FCSTD DOCUMENT  (FreeCAD 0.20R29177 +426 (Git))
Label: ASM_Base
License: All rights reserved
LicenseURL: http://en.wikipedia.org/wiki/All_rights_reserved
objects: App::Link×6, App::DocumentObjectGroup×3, PartDesign::CoordinateSystem×1, App::FeaturePython×1, App::Part×1
note: 1 computed .brp shape members not serialized (recipe doc carries the construction recipe); baked Part::Feature solids carry a one-line shape summary decoded from their .brp
EXTERNAL_REF file=CeilingPlate.FCStd obj=LCS_Origin
EXTERNAL_REF file=PipeFloorFlange.FCStd obj=LCS_1
EXTERNAL_REF file=PipeFloorFlange.FCStd obj=Body
EXTERNAL_REF file=PipeNipple.FCStd obj=LCS_root
EXTERNAL_REF file=PipeNipple.FCStd obj=Body
EXTERNAL_REF file=PipeNipple.FCStd obj=LCS_end
EXTERNAL_REF file=SlipRing.FCStd obj=LCS_Origin
EXTERNAL_REF file=SlipRing.FCStd obj=Assembly
EXTERNAL_REF file=CeilingPlate.FCStd obj=Assembly
EXTERNAL_REF file=CeilingPlate.FCStd obj=Pad
EXTERNAL_REF file=CeilingPlate.FCStd obj=Sketch001
EXTERNAL_REF file=StrutChannelHalf.FCStd obj=LCS_Face
EXTERNAL_REF file=StrutChannelHalf.FCStd obj=Assembly

FEATURE [App::DocumentObjectGroup] Parts
FEATURE [PartDesign::CoordinateSystem] LCS_Origin
  AttacherType = Attacher::AttachEngine3D
  MapMode = 2
  Support = -> [X_Axis]
FEATURE [App::FeaturePython] Variables  # WARN: FeaturePython — macro-defined, semantics opaque (R4)
  Type = App::PropertyContainer
FEATURE [App::DocumentObjectGroup] Constraints
FEATURE [App::DocumentObjectGroup] Configurations
FEATURE [App::Link] PipeFlange
  AssemblyType = Part::Link
  AttachedBy = #LCS_1
  AttachedTo = CeilingPlate#LCS_Origin
  AttachmentOffset = pos=(0,0,0) rot=(1,0,0;3.14159rad)
  LinkPlacement = pos=(0,0,0) rot=(1,0,0;3.14159rad)
  LinkedObject = -> <external PipeFloorFlange.FCStd>#Body
  Placement = pos=(0,0,0) rot=(1,0,0;3.14159rad)
  SolverId = Asm4EE
  expr: Placement = CeilingPlate.Placement * CeilingPlate#LCS_Origin.Placement * AttachmentOffset * PipeFloorFlange#LCS_1.Placement ^ -1
FEATURE [App::Link] PipeNipple
  AssemblyType = Part::Link
  AttachedBy = #LCS_root
  AttachedTo = PipeFlange#LCS_1
  LinkPlacement = pos=(0,0,0) rot=(1,0,0;3.14159rad)
  LinkedObject = -> <external PipeNipple.FCStd>#Body
  Placement = pos=(0,0,0) rot=(1,0,0;3.14159rad)
  SolverId = Asm4EE
  expr: Placement = PipeFlange.Placement * PipeFloorFlange#LCS_1.Placement * AttachmentOffset * PipeNipple#LCS_root.Placement ^ -1
FEATURE [App::Link] SlipRing
  AttachedBy = #LCS_Origin
  AttachedTo = PipeNipple#LCS_end
  AttachmentOffset = pos=(0,0,0) rot=(1,0,0;3.14159rad)
  LinkPlacement = pos=(0,-1.09e-14,-88.9) rot=(0,0,1;0rad)
  LinkedObject = -> <external SlipRing.FCStd>#Assembly
  Placement = pos=(0,-1.09e-14,-88.9) rot=(0,0,1;0rad)
  SolverId = Asm4EE
  expr: Placement = PipeNipple.Placement * PipeNipple#LCS_end.Placement * AttachmentOffset * SlipRing#LCS_Origin.Placement ^ -1
FEATURE [App::Link] CeilingPlate
  AttachedBy = #LCS_Origin
  AttachedTo = Parent Assembly#LCS_Origin
  LinkedObject = -> <external CeilingPlate.FCStd>#Assembly
  SolverId = Asm4EE
  expr: Placement = LCS_Origin.Placement * AttachmentOffset * CeilingPlate#LCS_Origin.Placement ^ -1
FEATURE [App::Link] StrutChannelHalf
  AttachedBy = #LCS_Face
  AttachedTo = Parent Assembly#LCS_Origin
  AttachmentOffset = pos=(135.057,0,18.5) rot=(1,0,0;4.71239rad)
  LinkPlacement = pos=(135.057,4.6e-15,39.14) rot=(1,0,0;4.71239rad)
  LinkedObject = -> <external StrutChannelHalf.FCStd>#Assembly
  Placement = pos=(135.057,4.6e-15,39.14) rot=(1,0,0;4.71239rad)
  SolverId = Asm4EE
  expr: .AttachmentOffset.Base.x = <<CeilingPlate>>#<<Sketch001>>.Constraints.CeilingRailSpacing / 2
  expr: .AttachmentOffset.Base.z = <<CeilingPlate>>#<<Pad>>.Length
  expr: Placement = LCS_Origin.Placement * AttachmentOffset * StrutChannelHalf#LCS_Face.Placement ^ -1
FEATURE [App::Link] StrutChannelHalf001
  AttachedBy = #LCS_Face
  AttachedTo = Parent Assembly#LCS_Origin
  AttachmentOffset = pos=(-135.057,0,18.5) rot=(1,0,0;4.71239rad)
  LinkPlacement = pos=(-135.057,4.6e-15,39.14) rot=(1,0,0;4.71239rad)
  LinkedObject = -> <external StrutChannelHalf.FCStd>#Assembly
  Placement = pos=(-135.057,4.6e-15,39.14) rot=(1,0,0;4.71239rad)
  SolverId = Asm4EE
  expr: .AttachmentOffset.Base.x = <<CeilingPlate>>#<<Sketch001>>.Constraints.CeilingRailSpacing / -2
  expr: .AttachmentOffset.Base.z = <<CeilingPlate>>#<<Pad>>.Length
  expr: Placement = LCS_Origin.Placement * AttachmentOffset * StrutChannelHalf#LCS_Face.Placement ^ -1
FEATURE [App::Part] Assembly
  AssemblyType = Part::Link
  Group = -> [LCS_Origin,Variables,Constraints,Configurations,PipeFlange,PipeNipple,SlipRing,CeilingPlate,StrutChannelHalf,StrutChannelHalf001]
  LabelDocUser = ASM_Base
  LabelPartUser = Assembly
  Origin = -> Origin
  Type = Assembly

RESOLVED EXTERNAL PARTS (link-assembly join: the EXTERNAL_REF files above that resolve inside this repo's crawl, each included once):
---- part CeilingPlate.FCStd = doc fcstd_5e722962f203 ----
FCSTD DOCUMENT  (FreeCAD 0.20R29177 +426 (Git))
Label: CeilingPlate
License: All rights reserved
LicenseURL: http://en.wikipedia.org/wiki/All_rights_reserved
objects: App::DocumentObjectGroup×4, Sketcher::SketchObject×2, Part::FeaturePython×2, PartDesign::CoordinateSystem×1, App::FeaturePython×1, PartDesign::Pad×1, PartDesign::Hole×1, PartDesign::Body×1, App::Part×1
note: 10 computed .brp shape members not serialized (recipe doc carries the construction recipe); baked Part::Feature solids carry a one-line shape summary decoded from their .brp
EXTERNAL_REF file=Params.FCStd obj=Spreadsheet

FEATURE [App::DocumentObjectGroup] Parts
FEATURE [PartDesign::CoordinateSystem] LCS_Origin
  AttacherType = Attacher::AttachEngine3D
  MapMode = 2
  Support = -> [X_Axis]
FEATURE [App::FeaturePython] Variables  # WARN: FeaturePython — macro-defined, semantics opaque (R4)
  Type = App::PropertyContainer
FEATURE [App::DocumentObjectGroup] Constraints
FEATURE [App::DocumentObjectGroup] Configurations
FEATURE [Sketcher::SketchObject] Sketch
  FullyConstrained = true
  MapMode = 5
  Support = -> [XY_Plane001]
  expr: .Constraints.Diameter = <<Params>>#<<Params>>.CeilingPlateDiameter
  sketch-geometry (2):
    g0: Circle CenterX=0 CenterY=0 CenterZ=0 NormalX=0 NormalY=0 NormalZ=1 AngleXU=0 Radius=12.5
    g1: Circle CenterX=0 CenterY=0 CenterZ=0 NormalX=0 NormalY=0 NormalZ=1 AngleXU=0 Radius=231.5
  constraints (4):
    c: Coincident(g0,g-1)
    c: Coincident(g1,g0)
    c: Diameter(g1) = 463  'Diameter'
    c: Diameter(g0) = 25
FEATURE [PartDesign::Pad] Pad
  Direction = (0,0,1)
  Length = 18.5
  Length2 = 10
  Profile = -> Sketch
  ReferenceAxis = -> Sketch [N_Axis]
  Type = 0
  expr: Length = <<Params>>#<<Params>>.PlywoodThickness
FEATURE [Sketcher::SketchObject] Sketch001
  FullyConstrained = true
  MapMode = 5
  Support = -> [XY_Plane001]
  expr: Constraints[15] = <<Params>>#<<Params>>.TableRollerDriveSupportRadius
  expr: Constraints[16] = <<Params>>#<<Params>>.TableRollerSideRadius
  sketch-geometry (12):
    g0: Circle CenterX=135.057 CenterY=135.057 CenterZ=0 NormalX=0 NormalY=0 NormalZ=1 AngleXU=0 Radius=2.5
    g1: LineSegment StartX=-135.057 StartY=-135.057 StartZ=0 EndX=-135.057 EndY=135.057 EndZ=0
    g2: LineSegment StartX=-135.057 StartY=135.057 StartZ=0 EndX=135.057 EndY=135.057 EndZ=0
    g3: LineSegment StartX=135.057 StartY=135.057 StartZ=0 EndX=135.057 EndY=-135.057 EndZ=0
    g4: LineSegment StartX=135.057 StartY=-135.057 StartZ=0 EndX=-135.057 EndY=-135.057 EndZ=0
    g5: GeomPoint X=0 Y=0 Z=0
    g6: Circle CenterX=0 CenterY=0 CenterZ=0 NormalX=0 NormalY=0 NormalZ=1 AngleXU=0 Radius=218
    g7: Circle CenterX=0 CenterY=0 CenterZ=0 NormalX=0 NormalY=0 NormalZ=1 AngleXU=0 Radius=164
    g8: LineSegment StartX=115.966 StartY=115.966 StartZ=0 EndX=154.149 EndY=154.149 EndZ=0
    g9: Circle CenterX=-135.057 CenterY=135.057 CenterZ=0 NormalX=0 NormalY=0 NormalZ=1 AngleXU=0 Radius=2.5
    g10: Circle CenterX=-135.057 CenterY=-135.057 CenterZ=0 NormalX=0 NormalY=0 NormalZ=1 AngleXU=0 Radius=2.5
    g11: Circle CenterX=135.057 CenterY=-135.057 CenterZ=0 NormalX=0 NormalY=0 NormalZ=1 AngleXU=0 Radius=2.5
  constraints (28):
    c: Coincident(g1,g2)
    c: Coincident(g2,g3)
    c: Coincident(g3,g4)
    c: Coincident(g4,g1)
    c: Horizontal(g2)
    c: Horizontal(g4)
    c: Vertical(g1)
    c: Vertical(g3)
    c: Symmetric(g2,g1,g5)
    c: Coincident(g5,g-1)
    c: Coincident(g2,g0)
    c: Equal(g3,g2)
    c: Diameter(g0) = 5
    c: Coincident(g6,g5)
    c: Coincident(g7,g5)
    c: Radius(g6) = 218
    c: Radius(g7) = 164
    c: PointOnObject(g8,g7)
    c: PointOnObject(g8,g6)
    c: PointOnObject(g5,g8)
    c: Symmetric(g8,g8,g0)
    c: Coincident(g9,g1)
    c: Coincident(g10,g1)
    c: Coincident(g11,g3)
    c: Equal(g10,g11)
    c: Equal(g11,g9)
    c: Equal(g9,g0)
    c: DistanceX(g2,g2) = 270.115  'CeilingRailSpacing'
FEATURE [PartDesign::Hole] Hole  label="MountHoles"
  BaseFeature = -> Pad
  CustomThreadClearance = 0
  Depth = 1342.04
  DepthType = 1
  Diameter = 10.3
  DrillForDepth = false
  DrillPoint = 1
  DrillPointAngle = 118
  HoleCutCountersinkAngle = 82
  HoleCutCustomValues = false
  HoleCutDepth = 1.5
  HoleCutDiameter = 20.3
  HoleCutType = 2
  ModelThread = false
  Profile = -> Sketch001
  Reversed = true
  Tapered = false
  TaperedAngle = 90
  ThreadClass = 0
  ThreadDepth = 1342.04
  ThreadDepthType = 0
  ThreadDirection = 0
  ThreadFit = 0
  ThreadSize = 11
  ThreadType = 3
  Threaded = false
  UseCustomThreadClearance = false
FEATURE [PartDesign::Body] Body
  Group = -> [Sketch,Pad,Sketch001,Hole]
  Origin = -> Origin001
  Tip = -> Hole
FEATURE [Part::FeaturePython] Screw  label="3/8inx1 1/4in-Screw"  # Fasteners workbench fastener (typed FeaturePython)
  Placement = pos=(135.057,-135.057,0) rot=(1,0,0;3.14159rad)
  baseObject = -> Sketch001 [Edge4]
  diameter = 12
  invert = true
  leftHanded = false
  length = 3
  lengthCustom = 31.75
  matchOuter = false
  offset = 0
  thread = false
  type = 3
FEATURE [Part::FeaturePython] Array_Screw  label="Array_3/8inx1 1/4in-Screw"  # Draft array (typed FeaturePython)
  ArraySteps = 0
  ArrayType = Circular Array
  Axis = LCS_Origin.Z
  Count = 4
  ElementCount = 4
  FullAngle = 360
  IntervalAngle = 90
  LinearSteps = 0
  PlacementList = 4 placements: [(135.057,-135.057,0),(135.057,135.057,0),(-135.057,135.057,0),(-135.057,-135.057,0)]
  ScaleList = (4) [(1,1,1),(1,1,1),(1,1,1),(1,1,1)]
  ShowElement = false
  SourceObject = -> Screw
FEATURE [App::DocumentObjectGroup] Fasteners
  Group = -> [Screw,Array_Screw]
FEATURE [App::Part] Assembly
  AssemblyType = Part::Link
  Group = -> [LCS_Origin,Variables,Constraints,Configurations,Body,Fasteners,Screw,Array_Screw]
  Origin = -> Origin
  Type = Assembly
---- part PipeFloorFlange.FCStd = doc fcstd_2355635570af ----
FCSTD DOCUMENT  (FreeCAD 0.20R29177 +426 (Git))
Label: PipeFloorFlange
License: All rights reserved
LicenseURL: http://en.wikipedia.org/wiki/All_rights_reserved
objects: Sketcher::SketchObject×2, PartDesign::Revolution×1, PartDesign::Hole×1, PartDesign::PolarPattern×1, PartDesign::CoordinateSystem×1, PartDesign::Body×1
note: 9 computed .brp shape members not serialized (recipe doc carries the construction recipe); baked Part::Feature solids carry a one-line shape summary decoded from their .brp

FEATURE [Sketcher::SketchObject] Sketch
  FullyConstrained = true
  MapMode = 5
  Placement = pos=(0,0,0) rot=(1,0,0;1.5708rad)
  Support = -> [XZ_Plane]
  sketch-geometry (6):
    g0: LineSegment StartX=14.86 StartY=0 StartZ=0 EndX=47.625 EndY=0 EndZ=0
    g1: LineSegment StartX=47.625 StartY=0 StartZ=0 EndX=47.625 EndY=8 EndZ=0
    g2: LineSegment StartX=47.625 StartY=8 StartZ=0 EndX=22.86 EndY=8 EndZ=0
    g3: LineSegment StartX=22.86 StartY=8 StartZ=0 EndX=22.86 EndY=17.78 EndZ=0
    g4: LineSegment StartX=22.86 StartY=17.78 StartZ=0 EndX=14.86 EndY=17.78 EndZ=0
    g5: LineSegment StartX=14.86 StartY=17.78 StartZ=0 EndX=14.86 EndY=0 EndZ=0
  constraints (18):
    c: PointOnObject(g0,g-1)
    c: Horizontal(g0)
    c: Coincident(g1,g0)
    c: Coincident(g2,g1)
    c: Horizontal(g2)
    c: Coincident(g3,g2)
    c: Vertical(g3)
    c: Coincident(g4,g3)
    c: Horizontal(g4)
    c: Vertical(g5)
    c: Coincident(g5,g4)
    c: Coincident(g5,g0)
    c: Vertical(g1)
    c: DistanceX(g-1,g3) = 22.86
    c: DistanceY(g1,g1) = 8  'Thickness'
    c: DistanceY(g5,g5) = 17.78
    c: DistanceX(g-1,g0) = 47.625
    c: DistanceX(g4,g4) = 8
FEATURE [PartDesign::Revolution] Revolution
  Angle = 360
  Axis = (0,-2e-16,1)
  Base = (0,0,0)
  Placement = pos=(0,0,0) rot=(1,0,0;1.5708rad)
  Profile = -> Sketch
  ReferenceAxis = -> Sketch [V_Axis]
  Reversed = true
FEATURE [Sketcher::SketchObject] Sketch001
  AttachmentOffset = pos=(0,0,8) rot=(0,0,1;0rad)
  FullyConstrained = true
  MapMode = 5
  Placement = pos=(0,0,8) rot=(0,0,1;0rad)
  Support = -> [XY_Plane]
  expr: .AttachmentOffset.Base.z = <<Sketch>>.Constraints.Thickness
  sketch-geometry (1):
    g0: Circle CenterX=0 CenterY=35 CenterZ=0 NormalX=0 NormalY=0 NormalZ=1 AngleXU=0 Radius=3
  constraints (3):
    c: PointOnObject(g0,g-2)
    c: DistanceY(g-1,g0) = 35
    c: Diameter(g0) = 6
FEATURE [PartDesign::Hole] Hole
  BaseFeature = -> Revolution
  CustomThreadClearance = 0
  Depth = 25
  DepthType = 0
  Diameter = 8.7
  DrillForDepth = false
  DrillPoint = 1
  DrillPointAngle = 118
  HoleCutCountersinkAngle = 82
  HoleCutCustomValues = false
  HoleCutDepth = 0
  HoleCutDiameter = 14.79
  HoleCutType = 2
  ModelThread = false
  Placement = pos=(0,0,0) rot=(1,0,0;1.5708rad)
  Profile = -> Sketch001
  Tapered = false
  TaperedAngle = 90
  ThreadClass = 0
  ThreadDepth = 25
  ThreadDepthType = 0
  ThreadDirection = 0
  ThreadFit = 0
  ThreadSize = 10
  ThreadType = 3
  Threaded = false
  UseCustomThreadClearance = false
FEATURE [PartDesign::PolarPattern] PolarPattern
  Angle = 360
  Axis = -> Sketch001 [N_Axis]
  BaseFeature = -> Hole
  Occurrences = 4
  Originals = -> [Hole]
  Placement = pos=(0,0,0) rot=(1,0,0;1.5708rad)
FEATURE [PartDesign::CoordinateSystem] LCS_1
  AttacherType = Attacher::AttachEngine3D
  MapMode = 2
  Support = -> [XY_Plane]
FEATURE [PartDesign::Body] Body
  Group = -> [Sketch,Revolution,Sketch001,Hole,PolarPattern,LCS_1]
  Origin = -> Origin
  Tip = -> PolarPattern
---- part PipeNipple.FCStd = doc fcstd_4dfc671c1cfc ----
FCSTD DOCUMENT  (FreeCAD 0.20R29177 +426 (Git))
Label: PipeNipple
License: All rights reserved
LicenseURL: http://en.wikipedia.org/wiki/All_rights_reserved
objects: PartDesign::CoordinateSystem×2, Sketcher::SketchObject×1, PartDesign::Pad×1, PartDesign::Body×1
note: 6 computed .brp shape members not serialized (recipe doc carries the construction recipe); baked Part::Feature solids carry a one-line shape summary decoded from their .brp

FEATURE [Sketcher::SketchObject] Sketch
  FullyConstrained = true
  MapMode = 5
  Support = -> [XY_Plane]
  sketch-geometry (2):
    g0: Circle CenterX=0 CenterY=0 CenterZ=0 NormalX=0 NormalY=0 NormalZ=1 AngleXU=0 Radius=13.3223
    g1: Circle CenterX=0 CenterY=0 CenterZ=0 NormalX=0 NormalY=0 NormalZ=1 AngleXU=0 Radius=16.7005
  constraints (4):
    c: Coincident(g0,g-1)
    c: Coincident(g1,g0)
    c: Diameter(g1) = 33.401
    c: Diameter(g0) = 26.6446
FEATURE [PartDesign::Pad] Pad
  Direction = (0,0,1)
  Length = 88.9
  Length2 = 10
  Profile = -> Sketch
  ReferenceAxis = -> Sketch [N_Axis]
  Type = 0
FEATURE [PartDesign::CoordinateSystem] LCS_root
  AttacherType = Attacher::AttachEngine3D
  MapMode = 2
  Support = -> [XY_Plane]
FEATURE [PartDesign::CoordinateSystem] LCS_end
  AttacherType = Attacher::AttachEngine3D
  AttachmentOffset = pos=(0,0,88.9) rot=(0,0,1;0rad)
  MapMode = 2
  Placement = pos=(0,0,88.9) rot=(0,0,1;0rad)
  Support = -> [LCS_root]
  expr: .AttachmentOffset.Base.z = <<Pad>>.Length
FEATURE [PartDesign::Body] Body
  Group = -> [Sketch,Pad,LCS_root,LCS_end]
  Origin = -> Origin
  Tip = -> Pad
---- part SlipRing.FCStd = doc fcstd_0743c411564a ----
FCSTD DOCUMENT  (FreeCAD 0.20R29177 +426 (Git))
Label: SlipRing
License: All rights reserved
LicenseURL: http://en.wikipedia.org/wiki/All_rights_reserved
objects: App::DocumentObjectGroup×3, PartDesign::CoordinateSystem×1, App::FeaturePython×1, Sketcher::SketchObject×1, PartDesign::Revolution×1, PartDesign::Body×1, App::Part×1
note: 5 computed .brp shape members not serialized (recipe doc carries the construction recipe); baked Part::Feature solids carry a one-line shape summary decoded from their .brp

FEATURE [App::DocumentObjectGroup] Parts
FEATURE [PartDesign::CoordinateSystem] LCS_Origin
  AttacherType = Attacher::AttachEngine3D
  MapMode = 2
  Support = -> [X_Axis]
FEATURE [App::FeaturePython] Variables  # WARN: FeaturePython — macro-defined, semantics opaque (R4)
  Type = App::PropertyContainer
FEATURE [App::DocumentObjectGroup] Constraints
FEATURE [App::DocumentObjectGroup] Configurations
FEATURE [Sketcher::SketchObject] Sketch
  FullyConstrained = true
  MapMode = 5
  Placement = pos=(0,0,0) rot=(1,0,0;1.5708rad)
  Support = -> [XZ_Plane001]
  sketch-geometry (14):
    g0: LineSegment StartX=0 StartY=38.6 StartZ=0 EndX=11 EndY=38.6 EndZ=0
    g1: LineSegment StartX=11 StartY=38.6 StartZ=0 EndX=11 EndY=0 EndZ=0
    g2: LineSegment StartX=11 StartY=0 StartZ=0 EndX=22.2 EndY=0 EndZ=0
    g3: LineSegment StartX=22.2 StartY=0 StartZ=0 EndX=22.2 EndY=-2.6 EndZ=0
    g4: LineSegment StartX=22.2 StartY=-2.6 StartZ=0 EndX=11 EndY=-2.6 EndZ=0
    g5: LineSegment StartX=11 StartY=-2.6 StartZ=0 EndX=11 EndY=-8.6 EndZ=0
    g6: LineSegment StartX=11 StartY=-8.6 StartZ=0 EndX=5 EndY=-8.6 EndZ=0
    g7: LineSegment StartX=5 StartY=-8.6 StartZ=0 EndX=5 EndY=-14.6 EndZ=0
    g8: LineSegment StartX=0 StartY=-14.6 StartZ=0 EndX=0 EndY=38.6 EndZ=0
    g9: LineSegment StartX=5 StartY=-14.6 StartZ=0 EndX=4 EndY=-14.6 EndZ=0
    g10: LineSegment StartX=4 StartY=-14.6 StartZ=0 EndX=0 EndY=-14.6 EndZ=0
    g11: LineSegment StartX=4 StartY=-14.6 StartZ=0 EndX=4 EndY=-30.6 EndZ=0
    g12: LineSegment StartX=4 StartY=-30.6 StartZ=0 EndX=0 EndY=-30.6 EndZ=0
    g13: LineSegment StartX=0 StartY=-30.6 StartZ=0 EndX=0 EndY=-14.6 EndZ=0
  constraints (41):
    c: PointOnObject(g0,g-2)
    c: Horizontal(g0)
    c: Coincident(g0,g1)
    c: Vertical(g1)
    c: Coincident(g1,g2)
    c: Horizontal(g2)
    c: Coincident(g2,g3)
    c: Vertical(g3)
    c: Coincident(g3,g4)
    c: Horizontal(g4)
    c: Coincident(g4,g5)
    c: Vertical(g5)
    c: Coincident(g5,g6)
    c: Coincident(g6,g7)
    c: Vertical(g7)
    c: Coincident(g7,g9)
    c: PointOnObject(g10,g-2)
    c: Coincident(g10,g8)
    c: Coincident(g8,g0)
    c: Horizontal(g6)
    c: DistanceX(g0,g0) = 11
    c: DistanceX(g-1,g3) = 22.2
    c: PointOnObject(g1,g5)
    c: DistanceX(g10,g9) = 5
    c: DistanceY(g7,g7) = 6
    c: DistanceY(g5,g5) = 6
    c: DistanceY(g3,g3) = 2.6
    c: DistanceY(g1,g1) = 38.6
    c: PointOnObject(g1,g-1)
    c: Coincident(g9,g10)
    c: Horizontal(g9)
    c: Horizontal(g10)
    c: Coincident(g11,g9)
    c: Vertical(g11)
    c: Coincident(g12,g11)
    c: PointOnObject(g12,g-2)
    c: Horizontal(g12)
    c: Coincident(g13,g12)
    c: Coincident(g13,g8)
    c: DistanceX(g12,g12) = 4
    c: DistanceY(g13,g13) = 16
FEATURE [PartDesign::Revolution] Revolution
  Angle = 360
  Axis = (0,-2e-16,1)
  Base = (0,0,0)
  Placement = pos=(0,0,0) rot=(1,0,0;1.5708rad)
  Profile = -> Sketch
  ReferenceAxis = -> Sketch [V_Axis]
  Reversed = true
FEATURE [PartDesign::Body] Body
  Group = -> [Sketch,Revolution]
  Origin = -> Origin001
  Tip = -> Revolution
FEATURE [App::Part] Assembly
  AssemblyType = Part::Link
  Group = -> [LCS_Origin,Variables,Constraints,Configurations,Body]
  Origin = -> Origin
  Type = Assembly
---- part StrutChannelHalf.FCStd = doc fcstd_f8280f6d5164 ----
FCSTD DOCUMENT  (FreeCAD 0.20R29177 +426 (Git))
Label: StrutChannelHalf
License: All rights reserved
LicenseURL: http://en.wikipedia.org/wiki/All_rights_reserved
objects: App::DocumentObjectGroup×3, PartDesign::CoordinateSystem×2, Sketcher::SketchObject×2, App::FeaturePython×1, PartDesign::Pad×1, PartDesign::Pocket×1, PartDesign::LinearPattern×1, PartDesign::Mirrored×1, PartDesign::MultiTransform×1, PartDesign::Body×1, App::Part×1
note: 12 computed .brp shape members not serialized (recipe doc carries the construction recipe); baked Part::Feature solids carry a one-line shape summary decoded from their .brp

FEATURE [App::DocumentObjectGroup] Parts
FEATURE [PartDesign::CoordinateSystem] LCS_Origin
  AttacherType = Attacher::AttachEngine3D
  MapMode = 2
  Support = -> [X_Axis]
FEATURE [App::FeaturePython] Variables  # WARN: FeaturePython — macro-defined, semantics opaque (R4)
  Length = 600
  Type = App::PropertyContainer
FEATURE [App::DocumentObjectGroup] Constraints
FEATURE [App::DocumentObjectGroup] Configurations
FEATURE [Sketcher::SketchObject] Sketch
  FullyConstrained = true
  MapMode = 5
  Support = -> [XY_Plane001]
  sketch-geometry (22):
    g0: ArcOfCircle CenterX=-15.875 CenterY=15.8775 CenterZ=0 NormalX=0 NormalY=0 NormalZ=1 AngleXU=0 Radius=4.7625 StartAngle=-5.3e-15 EndAngle=3.14159
    g1: ArcOfCircle CenterX=15.875 CenterY=15.8775 CenterZ=0 NormalX=0 NormalY=0 NormalZ=1 AngleXU=0 Radius=4.7625 StartAngle=1e-16 EndAngle=3.14159
    g2: LineSegment StartX=20.6375 StartY=15.8775 StartZ=0 EndX=20.6375 EndY=1.5 EndZ=0
    g3: ArcOfCircle CenterX=19.1375 CenterY=1.5 CenterZ=0 NormalX=0 NormalY=0 NormalZ=1 AngleXU=0 Radius=1.5 StartAngle=4.71239 EndAngle=6.28319
    g4: LineSegment StartX=19.1375 StartY=0 StartZ=0 EndX=-19.1375 EndY=0 EndZ=0
    g5: ArcOfCircle CenterX=-19.1375 CenterY=1.5 CenterZ=0 NormalX=0 NormalY=0 NormalZ=1 AngleXU=0 Radius=1.5 StartAngle=3.14159 EndAngle=4.71239
    g6: LineSegment StartX=-20.6375 StartY=1.5 StartZ=0 EndX=-20.6375 EndY=15.8775 EndZ=0
    g7: GeomPoint X=20.6375 Y=0 Z=0
    g8: ArcOfCircle CenterX=-15.875 CenterY=15.8775 CenterZ=0 NormalX=0 NormalY=0 NormalZ=1 AngleXU=0 Radius=2.86512 StartAngle=-8e-15 EndAngle=3.14159
    g9: ArcOfCircle CenterX=15.875 CenterY=15.8775 CenterZ=0 NormalX=0 NormalY=0 NormalZ=1 AngleXU=0 Radius=2.86512 StartAngle=1e-16 EndAngle=3.14159
    g10: LineSegment StartX=18.7401 StartY=15.8775 StartZ=0 EndX=18.7401 EndY=2.89738 EndZ=0
    g11: ArcOfCircle CenterX=17.7401 CenterY=2.89738 CenterZ=0 NormalX=0 NormalY=0 NormalZ=1 AngleXU=0 Radius=1 StartAngle=4.71239 EndAngle=6.28319
    g12: LineSegment StartX=17.7401 StartY=1.89738 StartZ=0 EndX=-17.7401 EndY=1.89738 EndZ=0
    g13: ArcOfCircle CenterX=-17.7401 CenterY=2.89738 CenterZ=0 NormalX=0 NormalY=0 NormalZ=1 AngleXU=0 Radius=1 StartAngle=3.14159 EndAngle=4.71239
    g14: LineSegment StartX=-18.7401 StartY=2.89738 StartZ=0 EndX=-18.7401 EndY=15.8775 EndZ=0
    g15: GeomPoint X=18.7401 Y=1.89738 Z=0
    g16: GeomPoint X=1.3e-15 Y=1.89738 Z=0
    g17: LineSegment StartX=1.3e-15 StartY=1.89738 StartZ=0 EndX=0 EndY=0 EndZ=0
    g18: LineSegment StartX=18.7401 StartY=15.8775 StartZ=0 EndX=20.6375 EndY=15.8775 EndZ=0
    g19: LineSegment StartX=-13.0099 StartY=15.8775 StartZ=0 EndX=-11.1125 EndY=15.8775 EndZ=0
    g20: LineSegment StartX=11.1125 StartY=15.8775 StartZ=0 EndX=13.0099 EndY=15.8775 EndZ=0
    g21: LineSegment StartX=-15.875 StartY=20.64 StartZ=0 EndX=15.875 EndY=20.64 EndZ=0
  constraints (54):
    c: Tangent(g1,g2) = 1.5708
    c: Tangent(g2,g3) = 1.5708
    c: Tangent(g3,g4) = 1.5708
    c: Tangent(g4,g5) = 1.5708
    c: Tangent(g5,g6) = 1.5708
    c: Tangent(g6,g0) = 1.5708
    c: Horizontal(g4)
    c: Vertical(g2)
    c: Vertical(g6)
    c: Equal(g0,g1)
    c: Equal(g3,g5)
    c: PointOnObject(g7,g2)
    c: PointOnObject(g7,g4)
    c: Symmetric(g4,g3,g-1)
    c: Radius(g3) = 1.5
    c: Radius(g1) = 4.7625
    c: Tangent(g9,g10) = 1.5708
    c: Tangent(g10,g11) = 1.5708
    c: Tangent(g11,g12) = 1.5708
    c: Tangent(g12,g13) = 1.5708
    c: Tangent(g13,g14) = 1.5708
    c: Tangent(g14,g8) = 1.5708
    c: Horizontal(g12)
    c: Vertical(g10)
    c: Vertical(g14)
    c: Equal(g8,g9)
    c: Equal(g11,g13)
    c: PointOnObject(g15,g10)
    c: PointOnObject(g15,g12)
    c: Symmetric(g12,g11,g16)
    c: Coincident(g17,g16)
    c: Coincident(g17,g-1)
    c: DistanceY(g17,g17) = 1.89738
    c: Coincident(g18,g9)
    c: PointOnObject(g18,g2)
    c: Horizontal(g18)
    c: Equal(g18,g17)
    c: Coincident(g9,g1)
    c: Coincident(g8,g0)
    c: PointOnObject(g9,g18)
    c: PointOnObject(g8,g18)
    c: PointOnObject(g1,g18)
    c: PointOnObject(g0,g18)
    c: Coincident(g19,g8)
    c: Coincident(g19,g0)
    c: Coincident(g20,g1)
    c: Coincident(g20,g9)
    c: PointOnObject(g8,g19)
    c: DistanceX(g5,g2) = 41.275
    c: PointOnObject(g21,g0)
    c: Horizontal(g21)
    c: Tangent(g21,g1) = 1.5708
    c: DistanceY(g17,g21) = 20.64  'Height'
    c: Radius(g11) = 1
FEATURE [PartDesign::Pad] Pad
  Direction = (0,0,1)
  Length = 600
  Length2 = 10
  Midplane = true
  Profile = -> Sketch
  ReferenceAxis = -> Sketch [N_Axis]
  Type = 0
  expr: Length = <<Variables>>.Length
FEATURE [Sketcher::SketchObject] Sketch001
  FullyConstrained = true
  MapMode = 5
  Placement = pos=(0,0,0) rot=(1,0,0;1.5708rad)
  Support = -> [XZ_Plane001]
  sketch-geometry (5):
    g0: ArcOfCircle CenterX=0 CenterY=7.14125 CenterZ=0 NormalX=0 NormalY=0 NormalZ=1 AngleXU=0 Radius=7.14375 StartAngle=2.416e-13 EndAngle=3.14159
    g1: ArcOfCircle CenterX=0 CenterY=-7.14125 CenterZ=0 NormalX=0 NormalY=0 NormalZ=1 AngleXU=0 Radius=7.14375 StartAngle=3.14159 EndAngle=6.28319
    g2: LineSegment StartX=-7.14375 StartY=7.14125 StartZ=0 EndX=-7.14375 EndY=-7.14125 EndZ=0
    g3: LineSegment StartX=7.14375 StartY=-7.14125 StartZ=0 EndX=7.14375 EndY=7.14125 EndZ=0
    g4: LineSegment StartX=0 StartY=14.285 StartZ=0 EndX=0 EndY=-14.285 EndZ=0
  constraints (13):
    c: Tangent(g0,g2) = -1.5708
    c: Tangent(g2,g1) = -1.5708
    c: Tangent(g1,g3) = -1.5708
    c: Tangent(g3,g0) = -1.5708
    c: Equal(g0,g1)
    c: PointOnObject(g0,g-2)
    c: Symmetric(g0,g1,g-1)
    c: Diameter(g0) = 14.2875
    c: PointOnObject(g4,g0)
    c: PointOnObject(g4,g1)
    c: PointOnObject(g4,g-2)
    c: PointOnObject(g4,g-2)
    c: DistanceY(g4,g4) = 28.57
FEATURE [PartDesign::Pocket] Pocket  label="MountSlot"
  BaseFeature = -> Pad
  Direction = (0,1,2e-16)
  Length = 3
  Length2 = 5
  Profile = -> Sketch001
  ReferenceAxis = -> Sketch001 [N_Axis]
  Type = 0
FEATURE [PartDesign::LinearPattern] LinearPattern
  Direction = -> Sketch001 [V_Axis]
  Length = 355.6
  Occurrences = 8
  expr: Length = (ceil(<<Variables>>.Length / 2 / 50.8) + 1) * 50.8
  expr: Occurrences = ceil(<<Variables>>.Length / 2 / 50.8) + 2
FEATURE [PartDesign::Mirrored] Mirrored
  MirrorPlane = -> Sketch001 [H_Axis]
FEATURE [PartDesign::MultiTransform] MultiTransform
  BaseFeature = -> Pocket
  Originals = -> [Pocket]
  Transformations = -> [LinearPattern,Mirrored]
FEATURE [PartDesign::Body] Body
  Group = -> [Sketch,Pad,Sketch001,Pocket,MultiTransform,LinearPattern,Mirrored]
  Origin = -> Origin001
  Tip = -> MultiTransform
FEATURE [PartDesign::CoordinateSystem] LCS_Face
  AttacherType = Attacher::AttachEngine3D
  AttachmentOffset = pos=(0,20.64,0) rot=(0,0,1;0rad)
  MapMode = 2
  Placement = pos=(0,20.64,0) rot=(0,0,1;0rad)
  Support = -> [LCS_Origin]
  expr: .AttachmentOffset.Base.y = <<Sketch>>.Constraints.Height
FEATURE [App::Part] Assembly
  AssemblyType = Part::Link
  Group = -> [LCS_Origin,Variables,Constraints,Configurations,Body,LCS_Face]
  Origin = -> Origin
  Type = Assembly
